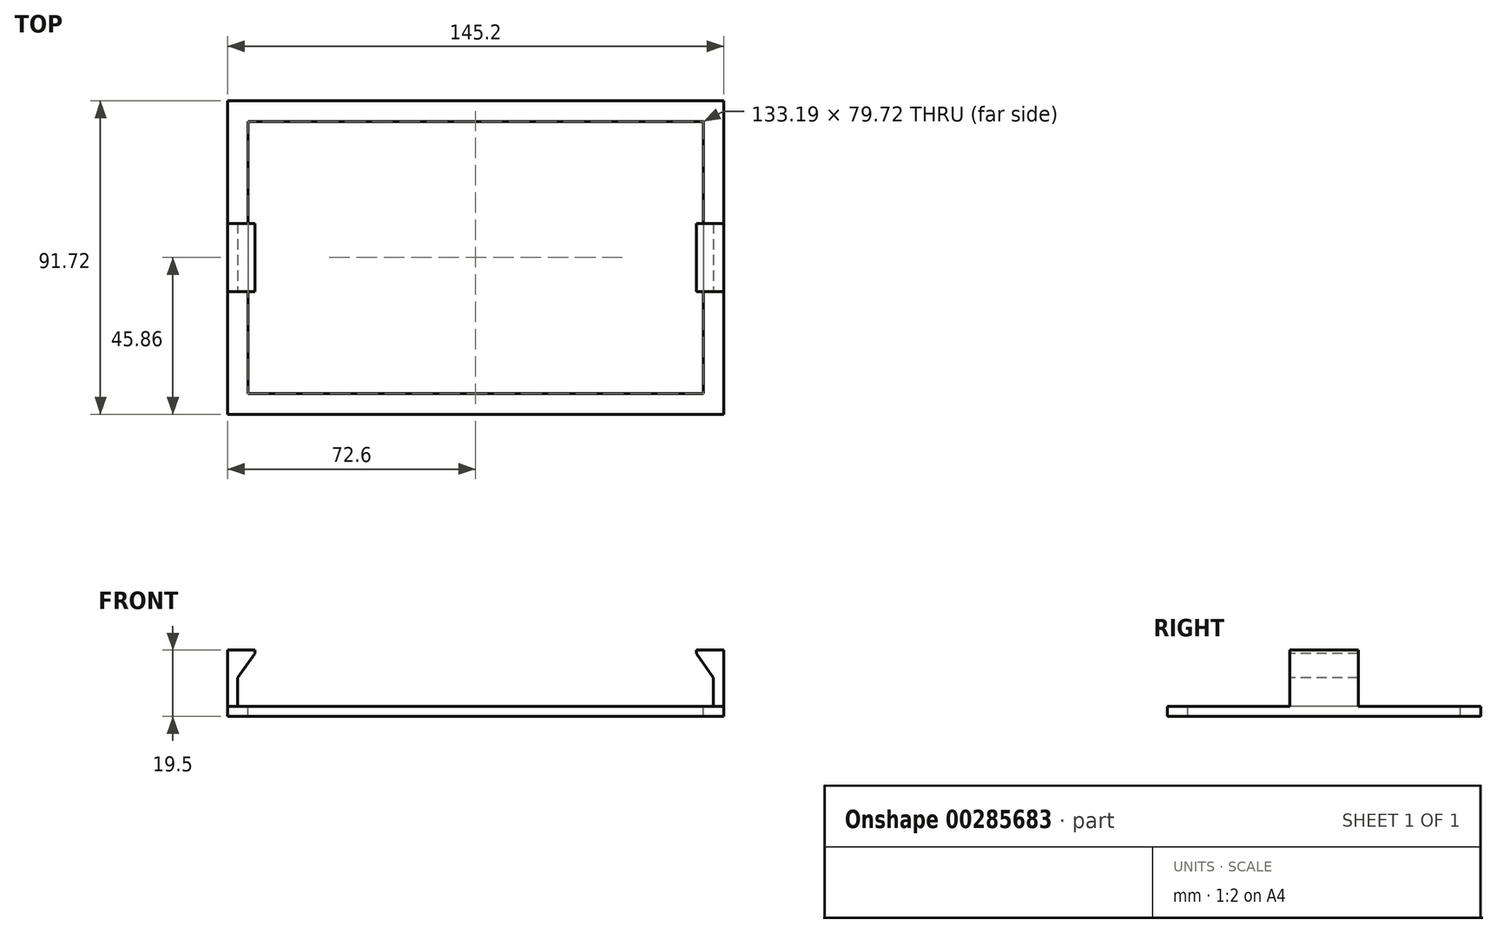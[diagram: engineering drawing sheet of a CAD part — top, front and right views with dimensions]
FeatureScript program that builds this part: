
annotation { "Feature Type Name" : "Feature", "Feature Type Description" : "" }
export const myFeature = defineFeature(function(context is Context, id is Id, definition is map)
    precondition{}
    {
        {
            var Q0;
            Q0=qCreatedBy(makeId("Top.planeOp"),FACE);
            var sketch = newSketch(context, id + "F0", { "sketchPlane" : qUnion([Q0])});
            skLineSegment(sketch, "E0.bottom", {"start": v(72.6, 45.86) * mm, "end": v(-72.6, 45.86) * mm});
            skLineSegment(sketch, "E0.top", {"start": v(72.6, -45.86) * mm, "end": v(-72.6, -45.86) * mm});
            skLineSegment(sketch, "E0.left", {"start": v(72.6, 45.86) * mm, "end": v(72.6, -45.86) * mm});
            skLineSegment(sketch, "E0.right", {"start": v(-72.6, 45.86) * mm, "end": v(-72.6, -45.86) * mm});
            skPoint(sketch, "E0.middle", {"position": v(0, 0) * mm});
            skSolve(sketch);
        }
        {
            var Q0;
            Q0=makeQuery(id+"F0.imprint","IMPRINT",FACE,{"disambiguationData":[TD([[makeQuery(id+"F0.imprint","IMPRINT",EDGE,{"derivedFrom":sQuery(id+"F0.wireOp",EDGE,"E0.bottom")}),1.0]])]});
            extrude(context, id + "F1", {"entities" : qUnion([Q0]), "depth" : 3 * mm});
        }
        {
            var Q0;
            Q0=makeQuery(id+"F1.opExtrude","CAP_FACE",FACE,{"disambiguationData":[OSD([sQuery(id+"F0.wireOp",EDGE,"E0.bottom"),sQuery(id+"F0.wireOp",EDGE,"E0.top"),sQuery(id+"F0.wireOp",EDGE,"E0.left"),sQuery(id+"F0.wireOp",EDGE,"E0.right")])],"isStart":false});
            var sketch = newSketch(context, id + "F2", { "sketchPlane" : qUnion([Q0])});
            skLineSegment(sketch, "E1.bottom", {"start": v(66.6, 39.86) * mm, "end": v(-66.6, 39.86) * mm});
            skLineSegment(sketch, "E1.top", {"start": v(66.6, -39.86) * mm, "end": v(-66.6, -39.86) * mm});
            skLineSegment(sketch, "E1.left", {"start": v(66.6, 39.86) * mm, "end": v(66.6, -39.86) * mm});
            skLineSegment(sketch, "E1.right", {"start": v(-66.6, 39.86) * mm, "end": v(-66.6, -39.86) * mm});
            skPoint(sketch, "E1.middle", {"position": v(0, 0) * mm});
            skSolve(sketch);
        }
        {
            var Q0;
            Q0=makeQuery(id+"F2.imprint","IMPRINT",FACE,{"disambiguationData":[TD([[makeQuery(id+"F2.imprint","IMPRINT",EDGE,{"derivedFrom":sQuery(id+"F2.wireOp",EDGE,"E1.bottom")}),1.0]])]});
            extrude(context, id + "F3", {"entities" : qUnion([Q0]), "operationType" : NewBodyOperationType.REMOVE, "oppositeDirection" : true, "depth" : 3 * mm});
        }
        {
            var Q0;
            Q0=makeQuery(id+"F1.opExtrude","CAP_FACE",FACE,{"disambiguationData":[OSD([sQuery(id+"F0.wireOp",EDGE,"E0.bottom"),sQuery(id+"F0.wireOp",EDGE,"E0.top"),sQuery(id+"F0.wireOp",EDGE,"E0.left"),sQuery(id+"F0.wireOp",EDGE,"E0.right")])],"isStart":false});
            var sketch = newSketch(context, id + "F4", { "sketchPlane" : qUnion([Q0])});
            skPoint(sketch, "E2.endSnap0", {"position": v(-72.6, 0) * mm});
            skLineSegment(sketch, "E3.bottom", {"start": v(-72.6, 10) * mm, "end": v(-69.6, 10) * mm});
            skLineSegment(sketch, "E3.top", {"start": v(-72.6, -10) * mm, "end": v(-69.6, -10) * mm});
            skLineSegment(sketch, "E3.left", {"start": v(-72.6, 10) * mm, "end": v(-72.6, -10) * mm});
            skLineSegment(sketch, "E3.right", {"start": v(-69.6, 10) * mm, "end": v(-69.6, -10) * mm});
            skSolve(sketch);
        }
        {
            var Q0;
            Q0=makeQuery(id+"F4.imprint","IMPRINT",FACE,{"disambiguationData":[TD([[makeQuery(id+"F4.imprint","IMPRINT",EDGE,{"derivedFrom":sQuery(id+"F4.wireOp",EDGE,"E3.bottom")}),-1.0]])]});
            extrude(context, id + "F5", {"entities" : qUnion([Q0]), "depth" : 16.5 * mm});
        }
        {
            var Q0;
            Q0=makeQuery(id+"F5.opExtrude","SWEPT_FACE",FACE,{"disambiguationData":[OSD([sQuery(id+"F4.wireOp",EDGE,"E3.top")])]});
            var sketch = newSketch(context, id + "F6", { "sketchPlane" : qUnion([Q0])});
            skLineSegment(sketch, "E4", {"start": v(-69.6, 19.5) * mm, "end": v(-64.6, 19.5) * mm});
            skLineSegment(sketch, "E5", {"start": v(-64.6, 19.5) * mm, "end": v(-64.6, 18.5) * mm});
            skLineSegment(sketch, "E6", {"start": v(-64.6, 18.5) * mm, "end": v(-69.6, 11.36) * mm});
            skSolve(sketch);
        }
        {
            var Q0;
            {var subQ0=sQuery(id+"F6.wireOp",EDGE,"E4");Q0=makeQuery(id+"F6.imprint","IMPRINT",FACE,{"disambiguationData":[TD([[makeQuery(id+"F6.imprint","IMPRINT",EDGE,{"derivedFrom":subQ0}),-1.0]])]});}
            extrude(context, id + "F7", {"entities" : qUnion([Q0]), "operationType" : NewBodyOperationType.ADD, "oppositeDirection" : true, "depth" : 20 * mm});
        }
        {
            var Q0;
            Q0=makeQuery(id+"F5.opExtrude","SWEPT_BODY",BODY,{"disambiguationData":[OSD([sQuery(id+"F4.wireOp",EDGE,"E3.bottom"),sQuery(id+"F4.wireOp",EDGE,"E3.top"),sQuery(id+"F4.wireOp",EDGE,"E3.left"),sQuery(id+"F4.wireOp",EDGE,"E3.right")])]});
            var Q1;
            Q1=qCreatedBy(makeId("Right.planeOp"),FACE);
            mirror(context, id + "F8", {"operationType" : NewBodyOperationType.ADD, "entities" : qUnion([Q0]), "mirrorPlane" : qUnion([Q1])});
        }
    });
